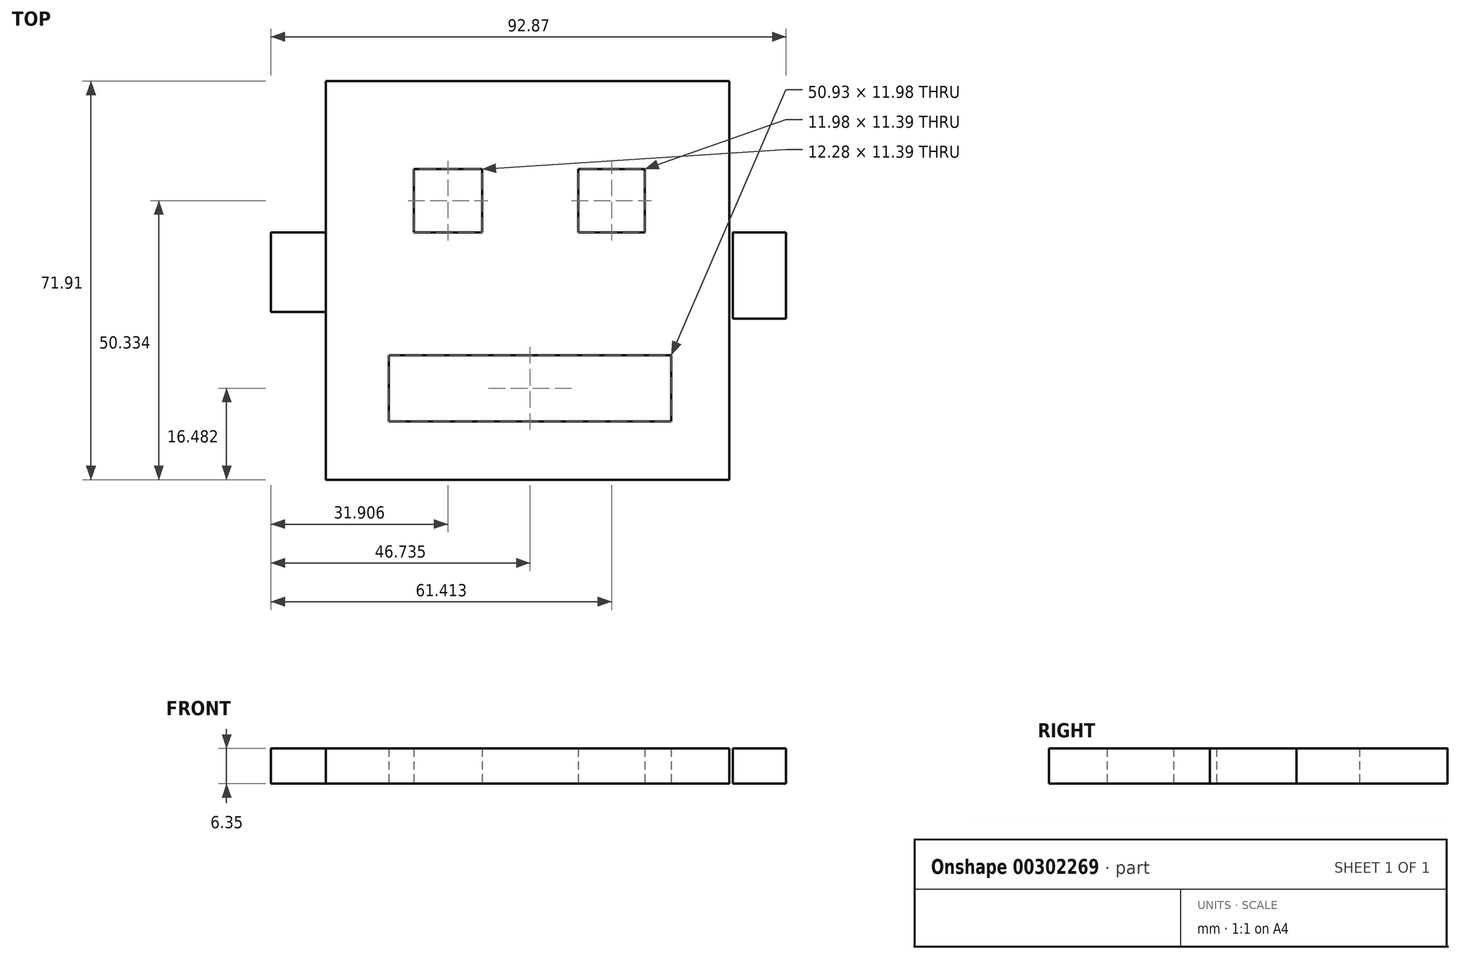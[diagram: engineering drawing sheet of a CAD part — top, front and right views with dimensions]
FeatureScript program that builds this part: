
annotation { "Feature Type Name" : "Feature", "Feature Type Description" : "" }
export const myFeature = defineFeature(function(context is Context, id is Id, definition is map)
    precondition{}
    {
        {
            var Q0;
            Q0=qCreatedBy(makeId("Top.planeOp"),FACE);
            var sketch = newSketch(context, id + "F0", { "sketchPlane" : qUnion([Q0])});
            skLineSegment(sketch, "E0.bottom", {"start": v(-21.3, 27.27) * mm, "end": v(51.5, 27.27) * mm});
            skLineSegment(sketch, "E0.top", {"start": v(-21.3, -44.64) * mm, "end": v(51.5, -44.64) * mm});
            skLineSegment(sketch, "E0.left", {"start": v(-21.3, 27.27) * mm, "end": v(-21.3, -44.64) * mm});
            skLineSegment(sketch, "E0.right", {"start": v(51.5, 27.27) * mm, "end": v(51.5, -44.64) * mm});
            skSolve(sketch);
        }
        {
            var Q0;
            Q0=qCreatedBy(makeId("Top.planeOp"),FACE);
            var sketch = newSketch(context, id + "F1", { "sketchPlane" : qUnion([Q0])});
            skLineSegment(sketch, "E1.bottom", {"start": v(52.1, 0) * mm, "end": v(61.69, 0) * mm});
            skLineSegment(sketch, "E1.top", {"start": v(52.1, -15.58) * mm, "end": v(61.69, -15.58) * mm});
            skLineSegment(sketch, "E1.left", {"start": v(52.1, 0) * mm, "end": v(52.1, -15.58) * mm});
            skLineSegment(sketch, "E1.right", {"start": v(61.69, 0) * mm, "end": v(61.69, -15.58) * mm});
            skSolve(sketch);
        }
        {
            var Q0;
            Q0=qCreatedBy(makeId("Top.planeOp"),FACE);
            var sketch = newSketch(context, id + "F2", { "sketchPlane" : qUnion([Q0])});
            skLineSegment(sketch, "E2.bottom", {"start": v(-21.3, 0) * mm, "end": v(-31.18, 0) * mm});
            skLineSegment(sketch, "E2.top", {"start": v(-21.3, -14.38) * mm, "end": v(-31.18, -14.38) * mm});
            skLineSegment(sketch, "E2.left", {"start": v(-21.3, 0) * mm, "end": v(-21.3, -14.38) * mm});
            skLineSegment(sketch, "E2.right", {"start": v(-31.18, 0) * mm, "end": v(-31.18, -14.38) * mm});
            skSolve(sketch);
        }
        {
            var Q0;
            Q0=qCreatedBy(makeId("Top.planeOp"),FACE);
            var sketch = newSketch(context, id + "F3", { "sketchPlane" : qUnion([Q0])});
            skLineSegment(sketch, "E3.bottom", {"start": v(-5.41, 11.39) * mm, "end": v(6.87, 11.39) * mm});
            skLineSegment(sketch, "E3.top", {"start": v(-5.41, 0) * mm, "end": v(6.87, 0) * mm});
            skLineSegment(sketch, "E3.left", {"start": v(-5.41, 11.39) * mm, "end": v(-5.41, 0) * mm});
            skLineSegment(sketch, "E3.right", {"start": v(6.87, 11.39) * mm, "end": v(6.87, 0) * mm});
            skLineSegment(sketch, "E4.bottom", {"start": v(24.24, 11.39) * mm, "end": v(36.22, 11.39) * mm});
            skLineSegment(sketch, "E4.top", {"start": v(24.24, 0) * mm, "end": v(36.22, 0) * mm});
            skLineSegment(sketch, "E4.left", {"start": v(24.24, 11.39) * mm, "end": v(24.24, 0) * mm});
            skLineSegment(sketch, "E4.right", {"start": v(36.22, 11.39) * mm, "end": v(36.22, 0) * mm});
            skSolve(sketch);
        }
        {
            var Q0;
            Q0=qCreatedBy(makeId("Top.planeOp"),FACE);
            var sketch = newSketch(context, id + "F4", { "sketchPlane" : qUnion([Q0])});
            skLineSegment(sketch, "E5.bottom", {"start": v(-9.9, -22.17) * mm, "end": v(41.02, -22.17) * mm});
            skLineSegment(sketch, "E5.top", {"start": v(-9.9, -34.15) * mm, "end": v(41.02, -34.15) * mm});
            skLineSegment(sketch, "E5.left", {"start": v(-9.9, -22.17) * mm, "end": v(-9.9, -34.15) * mm});
            skLineSegment(sketch, "E5.right", {"start": v(41.02, -22.17) * mm, "end": v(41.02, -34.15) * mm});
            skSolve(sketch);
        }
        {
            var Q0;
            Q0=makeQuery(id+"F0.imprint","IMPRINT",FACE,{"disambiguationData":[TD([[makeQuery(id+"F0.imprint","IMPRINT",EDGE,{"derivedFrom":sQuery(id+"F0.wireOp",EDGE,"E0.bottom")}),-1.0]])]});
            var Q1;
            Q1=makeQuery(id+"F1.imprint","IMPRINT",FACE,{"disambiguationData":[TD([[makeQuery(id+"F1.imprint","IMPRINT",EDGE,{"derivedFrom":sQuery(id+"F1.wireOp",EDGE,"E1.bottom")}),-1.0]])]});
            var Q2;
            Q2=makeQuery(id+"F2.imprint","IMPRINT",FACE,{"disambiguationData":[TD([[makeQuery(id+"F2.imprint","IMPRINT",EDGE,{"derivedFrom":sQuery(id+"F2.wireOp",EDGE,"E2.bottom")}),1.0]])]});
            extrude(context, id + "F5", {"entities" : qUnion([Q0, Q1, Q2]), "depth" : 6.35 * mm});
        }
        {
            var Q0;
            Q0=makeQuery(id+"F3.imprint","IMPRINT",FACE,{"disambiguationData":[TD([[makeQuery(id+"F3.imprint","IMPRINT",EDGE,{"derivedFrom":sQuery(id+"F3.wireOp",EDGE,"E3.bottom")}),-1.0]])]});
            var Q1;
            Q1=makeQuery(id+"F3.imprint","IMPRINT",FACE,{"disambiguationData":[TD([[makeQuery(id+"F3.imprint","IMPRINT",EDGE,{"derivedFrom":sQuery(id+"F3.wireOp",EDGE,"E4.bottom")}),-1.0]])]});
            extrude(context, id + "F6", {"entities" : qUnion([Q0, Q1]), "operationType" : NewBodyOperationType.REMOVE, "oppositeDirection" : true, "depth" : 25.4 * mm});
        }
        {
            var Q0;
            Q0=makeQuery(id+"F3.imprint","IMPRINT",FACE,{"disambiguationData":[TD([[makeQuery(id+"F3.imprint","IMPRINT",EDGE,{"derivedFrom":sQuery(id+"F3.wireOp",EDGE,"E4.bottom")}),-1.0]])]});
            var Q1;
            Q1=makeQuery(id+"F3.imprint","IMPRINT",FACE,{"disambiguationData":[TD([[makeQuery(id+"F3.imprint","IMPRINT",EDGE,{"derivedFrom":sQuery(id+"F3.wireOp",EDGE,"E3.bottom")}),-1.0]])]});
            extrude(context, id + "F7", {"entities" : qUnion([Q0, Q1]), "operationType" : NewBodyOperationType.ADD, "depth" : 6.35 * mm});
        }
        {
            var Q0;
            Q0=makeQuery(id+"F3.imprint","IMPRINT",FACE,{"disambiguationData":[TD([[makeQuery(id+"F3.imprint","IMPRINT",EDGE,{"derivedFrom":sQuery(id+"F3.wireOp",EDGE,"E4.bottom")}),-1.0]])]});
            var Q1;
            Q1=makeQuery(id+"F3.imprint","IMPRINT",FACE,{"disambiguationData":[TD([[makeQuery(id+"F3.imprint","IMPRINT",EDGE,{"derivedFrom":sQuery(id+"F3.wireOp",EDGE,"E3.bottom")}),-1.0]])]});
            extrude(context, id + "F8", {"entities" : qUnion([Q0, Q1]), "operationType" : NewBodyOperationType.REMOVE, "depth" : 25.4 * mm});
        }
        {
            var Q0;
            Q0=makeQuery(id+"F4.imprint","IMPRINT",FACE,{"disambiguationData":[TD([[makeQuery(id+"F4.imprint","IMPRINT",EDGE,{"derivedFrom":sQuery(id+"F4.wireOp",EDGE,"E5.bottom")}),-1.0]])]});
            extrude(context, id + "F9", {"entities" : qUnion([Q0]), "operationType" : NewBodyOperationType.REMOVE, "depth" : 25.4 * mm});
        }
    });
